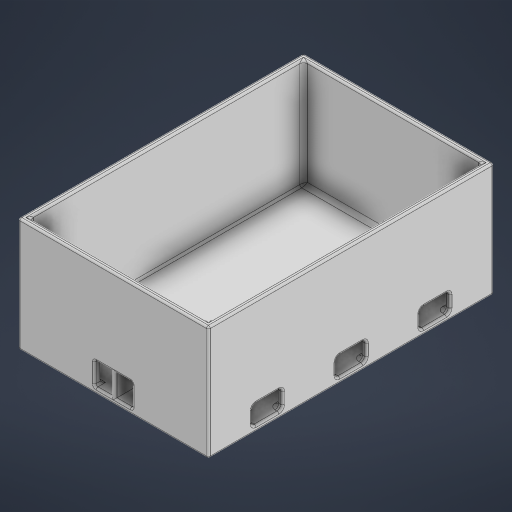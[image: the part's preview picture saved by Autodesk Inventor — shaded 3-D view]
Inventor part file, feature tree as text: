
AUTODESK INVENTOR PART (.ipt)
format: ipt  version: 2024.2 (Build 282272000, 272)  size: 519,680 bytes
history: native  units: mm
features: extrude x8, sketch x7, fillet x4, projected_geometry x4
ambient origin geometry x8: Origin, YZ Plane, XZ Plane, XY Plane, X Axis, Y Axis, Z Axis, Center Point
bodies: Solid1 (feature_tree)
feature tree (23):
  sketch  "Sketch1"  dims[d0=100.0mm d1=150.0mm]
  extrude  "Extrusion1"  Depth=150.0mm
  extrude  "Extrusion2"  Depth=3.0mm
  extrude  "Extrusion3"  Depth=3.0mm
  fillet  "Fillet1"  Radius=3.0mm
  extrude  "Extrusion4"  Depth=20.0mm
  extrude  "Extrusion5"  Depth=50.0mm
  extrude  "Extrusion6"  Depth=1.0mm
  extrude  "Extrusion7"  Depth=2.0mm
  extrude  "Extrusion8"  Depth=10.0mm
  fillet  "Fillet2"  Radius=5.0mm
  fillet  "Fillet3"  Radius=3.0mm
  fillet  "Fillet4"  Radius=16.0mm
  sketch  "Sketch2"  dims[d2=3.0mm d3=3.0mm]
  sketch  "Sketch3"  dims[d4=3.0mm d5=3.0mm d6=3.0mm d7=0.0mm]
  projected_geometry  "Projected Loop1"
  sketch  "Sketch4"  dims[d8=60.0mm d9=0.0mm d10=20.0mm]
  projected_geometry  "Projected Loop2"
  sketch  "Sketch5"  dims[d11=12.0mm d12=50.0mm]
  projected_geometry  "Projected Loop3"
  sketch  "Sketch6"  dims[d13=60.0mm d14=0.0mm d15=1.0mm]
  sketch  "Sketch7"  dims[d16=2.0mm d17=15.0mm d18=10.0mm d19=5.0mm d20=0.0mm d21=3.0mm d22=0.0mm d23=16.0mm d24=10.0mm d25=2.0mm d26=16.0mm d27=10.0mm d28=2.0mm d29=0.0mm d30=16.0mm d31=10.0mm d32=2.0mm d33=0.0mm d34=20.0mm d35=20.0mm d36=75.0mm d37=3.0mm d38=0.0mm d39=9.25mm d40=3.75mm d41=0.5mm d42=0.0mm d43=47.0mm d44=3.0mm d45=0.0mm d46=12.0mm d47=0.0mm d48=1.0mm d49=1.0mm d50=2.0mm]
  projected_geometry  "Projected Loop4"
